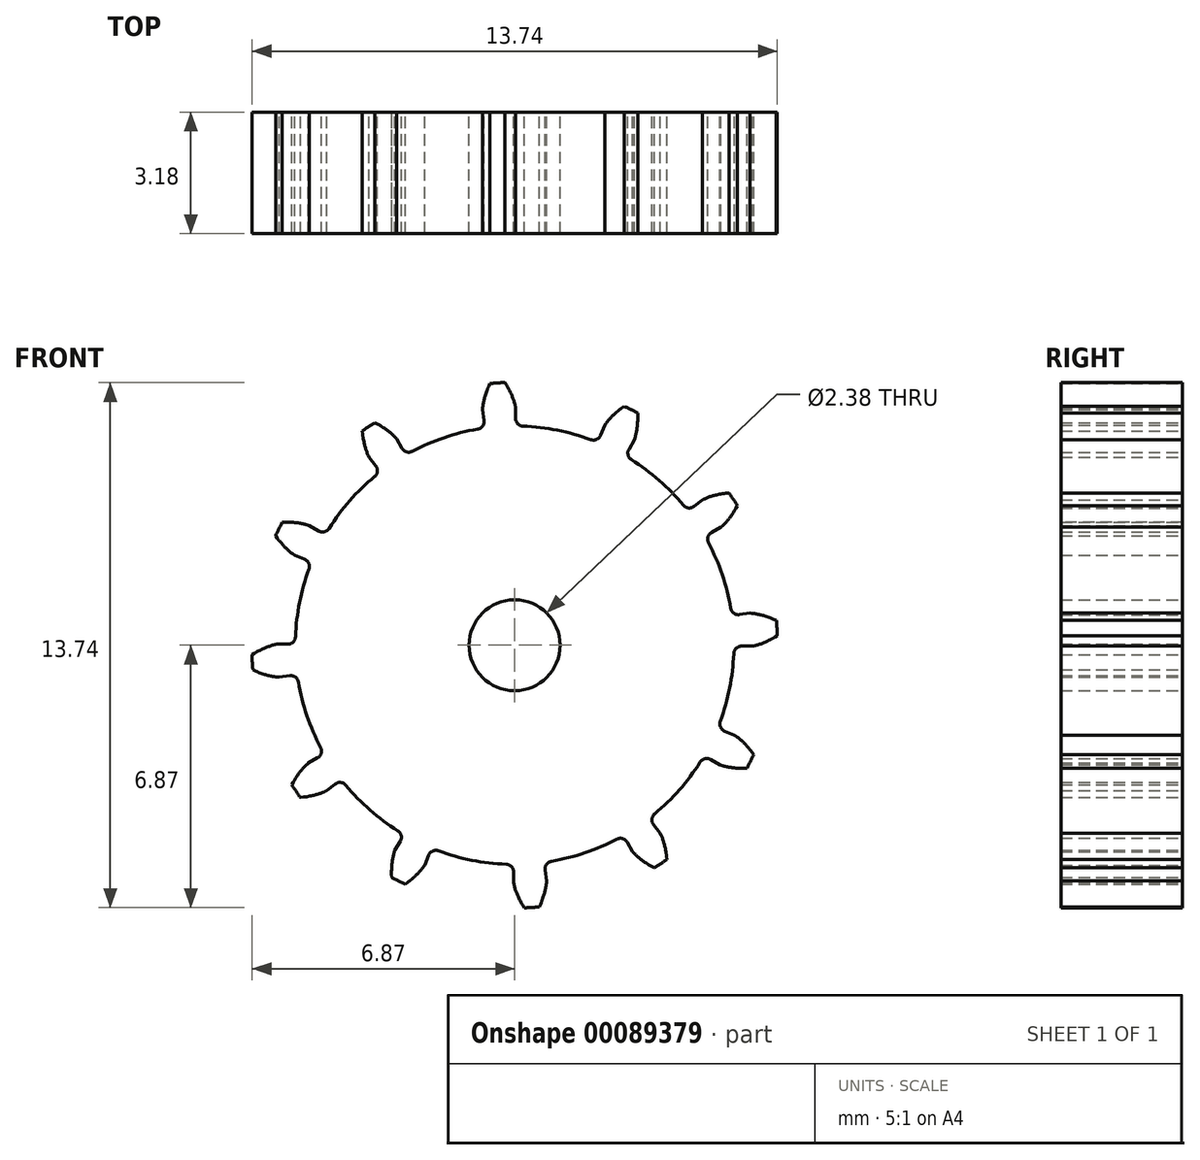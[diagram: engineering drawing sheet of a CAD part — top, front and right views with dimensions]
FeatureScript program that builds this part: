
annotation { "Feature Type Name" : "Feature", "Feature Type Description" : "" }
export const myFeature = defineFeature(function(context is Context, id is Id, definition is map)
    precondition{}
    {
        {
            assignVariable(context, id + "F0", {"name" : "Teeth", "anyValue" : 12});
        }
        {
            var Q0;
            Q0=qCreatedBy(makeId("Front.planeOp"),FACE);
            var sketch = newSketch(context, id + "F1", { "sketchPlane" : qUnion([Q0])});
            skCircle(sketch, "E0", {"center": v(0, 0) * mm, "radius": 6.15 * mm, "construction": true});
            skLineSegment(sketch, "E1", {"start": v(0, 0) * mm, "end": v(-0.28, 6.14) * mm, "construction": true});
            skLineSegment(sketch, "E2", {"start": v(0, 0) * mm, "end": v(-0.59, 6.12) * mm, "construction": true});
            skLineSegment(sketch, "E3", {"start": v(0, 0) * mm, "end": v(-0.9, 6.08) * mm, "construction": true});
            skLineSegment(sketch, "E4", {"start": v(-0.9, 6.08) * mm, "end": v(0.03, 6.22) * mm, "construction": true});
            skLineSegment(sketch, "E5", {"start": v(0, 0) * mm, "end": v(-1.2, 6.03) * mm, "construction": true});
            skLineSegment(sketch, "E6", {"start": v(-1.2, 6.03) * mm, "end": v(0.02, 6.27) * mm, "construction": true});
            skLineSegment(sketch, "E7", {"start": v(-0.9, 6.08) * mm, "end": v(-0.59, 6.12) * mm, "construction": true});
            skLineSegment(sketch, "E8", {"start": v(-1.2, 6.03) * mm, "end": v(-0.9, 6.08) * mm, "construction": true});
            skLineSegment(sketch, "E9", {"start": v(-0.9, 6.08) * mm, "end": v(-0.28, 6.14) * mm, "construction": true});
            skLineSegment(sketch, "E10", {"start": v(-1.2, 6.03) * mm, "end": v(-0.28, 6.14) * mm, "construction": true});
            skLineSegment(sketch, "E11", {"start": v(0, 0) * mm, "end": v(-2.1, 5.78) * mm, "construction": true});
            skLineSegment(sketch, "E12", {"start": v(-2.1, 5.78) * mm, "end": v(-0.07, 6.52) * mm, "construction": true});
            skLineSegment(sketch, "E13", {"start": v(0, 0) * mm, "end": v(-1.81, 5.87) * mm, "construction": true});
            skLineSegment(sketch, "E14", {"start": v(-1.81, 5.87) * mm, "end": v(-0.03, 6.42) * mm, "construction": true});
            skLineSegment(sketch, "E15", {"start": v(0, 0) * mm, "end": v(-1.51, 5.96) * mm, "construction": true});
            skLineSegment(sketch, "E16", {"start": v(-1.51, 5.96) * mm, "end": v(0, 6.34) * mm, "construction": true});
            skLineSegment(sketch, "E17", {"start": v(-1.51, 5.96) * mm, "end": v(-1.2, 6.03) * mm, "construction": true});
            skLineSegment(sketch, "E18", {"start": v(-1.51, 5.96) * mm, "end": v(-1.81, 5.87) * mm, "construction": true});
            skLineSegment(sketch, "E19", {"start": v(-1.81, 5.87) * mm, "end": v(-2.1, 5.78) * mm, "construction": true});
            skLineSegment(sketch, "E20", {"start": v(-1.51, 5.96) * mm, "end": v(-0.28, 6.14) * mm, "construction": true});
            skLineSegment(sketch, "E21", {"start": v(-1.81, 5.87) * mm, "end": v(-0.28, 6.14) * mm, "construction": true});
            skLineSegment(sketch, "E22", {"start": v(-2.1, 5.78) * mm, "end": v(-0.28, 6.14) * mm, "construction": true});
            skLineSegment(sketch, "E23", {"start": v(0, 0) * mm, "end": v(-2.68, 5.53) * mm, "construction": true});
            skLineSegment(sketch, "E24", {"start": v(-2.68, 5.53) * mm, "end": v(-0.18, 6.75) * mm, "construction": true});
            skLineSegment(sketch, "E25", {"start": v(0, 0) * mm, "end": v(-2.96, 5.39) * mm, "construction": true});
            skLineSegment(sketch, "E26", {"start": v(-2.96, 5.39) * mm, "end": v(-0.25, 6.87) * mm, "construction": true});
            skLineSegment(sketch, "E27", {"start": v(0, 0) * mm, "end": v(-3.23, 5.23) * mm, "construction": true});
            skLineSegment(sketch, "E28", {"start": v(0, 0) * mm, "end": v(-2.4, 5.66) * mm, "construction": true});
            skLineSegment(sketch, "E29", {"start": v(-2.4, 5.66) * mm, "end": v(-0.11, 6.63) * mm, "construction": true});
            skLineSegment(sketch, "E30", {"start": v(-2.1, 5.78) * mm, "end": v(-2.4, 5.66) * mm, "construction": true});
            skLineSegment(sketch, "E31", {"start": v(-2.4, 5.66) * mm, "end": v(-2.68, 5.53) * mm, "construction": true});
            skLineSegment(sketch, "E32", {"start": v(-2.68, 5.53) * mm, "end": v(-2.96, 5.39) * mm, "construction": true});
            skLineSegment(sketch, "E33", {"start": v(-2.96, 5.39) * mm, "end": v(-3.23, 5.23) * mm, "construction": true});
            skLineSegment(sketch, "E34", {"start": v(-0.28, 6.14) * mm, "end": v(-2.4, 5.66) * mm, "construction": true});
            skLineSegment(sketch, "E35", {"start": v(-0.28, 6.14) * mm, "end": v(-2.68, 5.53) * mm, "construction": true});
            skLineSegment(sketch, "E36", {"start": v(-0.28, 6.14) * mm, "end": v(-2.96, 5.39) * mm, "construction": true});
            skLineSegment(sketch, "E37", {"start": v(-0.28, 6.14) * mm, "end": v(-3.23, 5.23) * mm, "construction": true});
            skCircle(sketch, "E38", {"center": v(0, 0) * mm, "radius": 6.35 * mm, "construction": true});
            skCircle(sketch, "E39", {"center": v(0, 0) * mm, "radius": 6.88 * mm});
            skPoint(sketch, "E40", {"position": v(0, 6.35) * mm});
            skLineSegment(sketch, "E41", {"start": v(0, 0) * mm, "end": v(-0.56, 8.58) * mm, "construction": true});
            skPoint(sketch, "E42.MirrorP", {"position": v(-0.83, 6.3) * mm});
            skLineSegment(sketch, "E43", {"start": v(-0.83, 6.3) * mm, "end": v(0, 0) * mm, "construction": true});
            skLineSegment(sketch, "E44", {"start": v(0, 0) * mm, "end": v(0, 6.35) * mm, "construction": true});
            skLineSegment(sketch, "E45", {"start": v(-0.59, 6.12) * mm, "end": v(-0.28, 6.14) * mm, "construction": true});
            skLineSegment(sketch, "E46", {"start": v(0.03, 6.22) * mm, "end": v(0.02, 6.27) * mm, "construction": true});
            skLineSegment(sketch, "E47", {"start": v(0, 0) * mm, "end": v(0, 10.19) * mm, "construction": true});
            skCircle(sketch, "E48", {"center": v(0, 0) * mm, "radius": 5.74 * mm});
            skSolve(sketch);
        }
        {
            var Q0;
            Q0=qCreatedBy(makeId("Front.planeOp"),FACE);
            var sketch = newSketch(context, id + "F2", { "sketchPlane" : qUnion([Q0])});
            skCircle(sketch, "E49.0", {"center": v(0, 0) * mm, "radius": 6.35 * mm, "construction": true});
            skPoint(sketch, "E50.0", {"position": v(-0.25, 6.87) * mm});
            skPoint(sketch, "E50.1", {"position": v(-0.18, 6.75) * mm});
            skPoint(sketch, "E50.2", {"position": v(-0.11, 6.63) * mm});
            skPoint(sketch, "E50.3", {"position": v(-0.07, 6.52) * mm});
            skPoint(sketch, "E50.4", {"position": v(-0.03, 6.42) * mm});
            skPoint(sketch, "E50.6", {"position": v(0.02, 6.27) * mm});
            skPoint(sketch, "E50.7", {"position": v(0.03, 6.22) * mm});
            skPoint(sketch, "E50.8", {"position": v(0, 6.34) * mm});
            skLineSegment(sketch, "E51.0", {"start": v(0, 0) * mm, "end": v(-0.56, 8.58) * mm, "construction": true});
            skFitSpline(sketch, "E52", {"points": [v(-0.25, 6.87) * mm, v(-0.18, 6.75) * mm, v(-0.11, 6.63) * mm, v(-0.07, 6.52) * mm, v(-0.03, 6.42) * mm, v(0, 6.34) * mm, v(0.02, 6.27) * mm, v(0.03, 6.22) * mm], "startDerivative": vector(1.31, -2.2) * mm, "endDerivative": vector(0.3, -1.53) * mm});
            skFitSpline(sketch, "E53.MirrorCS", {"points": [v(-0.65, 6.85) * mm, v(-0.7, 6.71) * mm, v(-0.75, 6.59) * mm, v(-0.79, 6.47) * mm, v(-0.8, 6.37) * mm, v(-0.83, 6.29) * mm, v(-0.83, 6.22) * mm, v(-0.84, 6.16) * mm], "startDerivative": vector(-1.01, -2.36) * mm, "endDerivative": vector(-0.1, -1.56) * mm});
            skCircle(sketch, "E54", {"center": v(0, 0) * mm, "radius": 1.2 * mm});
            skCircle(sketch, "E55.0", {"center": v(0, 0) * mm, "radius": 5.74 * mm});
            skArc(sketch, "E56", {"start": v(-0.25, 6.87) * mm, "mid": v(-0.45, 6.86) * mm, "end": v(-0.65, 6.85) * mm});
            skLineSegment(sketch, "E57", {"start": v(-0.84, 6.16) * mm, "end": v(0, 0) * mm});
            skLineSegment(sketch, "E58", {"start": v(0, 0) * mm, "end": v(0.03, 6.22) * mm});
            skSolve(sketch);
        }
        {
            var Q0;
            {var subQ1=sQuery(id+"F2.wireOp",EDGE,"E52");var subQ9=sQuery(id+"F2.wireOp",EDGE,"rA0usyOi-Jm6w-jZNR-JSDv-ujEcH4bsm2Ol");var subQ11=makeQuery(id+"F2.imprint","INTERSECT",VERTEX,{"derivedFrom":[subQ1,subQ9]});Q0=makeQuery(id+"F2.imprint","IMPRINT",FACE,{"disambiguationData":[TD([[makeQuery(id+"F2.imprint","IMPRINT",EDGE,{"disambiguationData":[TD([[subQ11,1.0]])],"derivedFrom":subQ1}),-1.0]])]});}
            var Q1;
            {var subQ0=sQuery(id+"F2.wireOp",EDGE,"QqPcIgQ4-TZE6-73E5-WQaq-ugCT5JtziKyn");var subQ1=sQuery(id+"F2.wireOp",EDGE,"90be38e0-c88f-493d-85a8-1201295b9109.0");var subQ2=makeQuery(id+"F2.imprint","INTERSECT",VERTEX,{"derivedFrom":[subQ1,subQ0]});Q1=makeQuery(id+"F2.imprint","IMPRINT",FACE,{"disambiguationData":[TD([[makeQuery(id+"F2.imprint","IMPRINT",EDGE,{"disambiguationData":[TD([[subQ2,1.0]])],"derivedFrom":subQ1}),1.0]])]});}
            var Q2;
            {var subQ0=sQuery(id+"F2.wireOp",EDGE,"QqPcIgQ4-TZE6-73E5-WQaq-ugCT5JtziKyn");var subQ1=sQuery(id+"F2.wireOp",EDGE,"90be38e0-c88f-493d-85a8-1201295b9109.0");var subQ2=makeQuery(id+"F2.imprint","INTERSECT",VERTEX,{"derivedFrom":[subQ1,subQ0]});Q2=makeQuery(id+"F2.imprint","IMPRINT",FACE,{"disambiguationData":[TD([[makeQuery(id+"F2.imprint","IMPRINT",EDGE,{"disambiguationData":[TD([[subQ2,-1.0]])],"derivedFrom":subQ1}),1.0]])]});}
            var Q3;
            {var subQ1=sQuery(id+"F2.wireOp",EDGE,"E52");var subQ8=sQuery(id+"F2.wireOp",EDGE,"b861a5ab-cd51-40f1-92ab-cea0f5fe0d4d.1");var subQ11=makeQuery(id+"F2.imprint","INTERSECT",VERTEX,{"derivedFrom":[subQ1,subQ8]});Q3=makeQuery(id+"F2.imprint","IMPRINT",FACE,{"disambiguationData":[TD([[makeQuery(id+"F2.imprint","IMPRINT",EDGE,{"disambiguationData":[TD([[subQ11,1.0]])],"derivedFrom":subQ1}),-1.0]])]});}
            var Q4;
            {var subQ0=sQuery(id+"F2.wireOp",EDGE,"b861a5ab-cd51-40f1-92ab-cea0f5fe0d4d.0");var subQ1=sQuery(id+"F2.wireOp",EDGE,"E54");var subQ2=makeQuery(id+"F2.imprint","INTERSECT",VERTEX,{"derivedFrom":[subQ1,subQ0]});Q4=makeQuery(id+"F2.imprint","IMPRINT",FACE,{"disambiguationData":[TD([[makeQuery(id+"F2.imprint","IMPRINT",EDGE,{"disambiguationData":[TD([[subQ2,-1.0]])],"derivedFrom":subQ1}),-1.0]])]});}
            var Q5;
            {var subQ0=sQuery(id+"F2.wireOp",EDGE,"b861a5ab-cd51-40f1-92ab-cea0f5fe0d4d.0");var subQ1=sQuery(id+"F2.wireOp",EDGE,"E54");var subQ2=makeQuery(id+"F2.imprint","INTERSECT",VERTEX,{"derivedFrom":[subQ1,subQ0]});Q5=makeQuery(id+"F2.imprint","IMPRINT",FACE,{"disambiguationData":[TD([[makeQuery(id+"F2.imprint","IMPRINT",EDGE,{"disambiguationData":[TD([[subQ2,1.0]])],"derivedFrom":subQ1}),-1.0]])]});}
            extrude(context, id + "F3", {"entities" : qUnion([Q0, Q1, Q2, Q3, Q4, Q5]), "depth" : 3.17 * mm});
        }
        {
            var Q0;
            Q0=makeQuery(id+"F3.opExtrude","SWEPT_EDGE",EDGE,{"disambiguationData":[OSD([sQuery(id+"F2.wireOp",EDGE,"b861a5ab-cd51-40f1-92ab-cea0f5fe0d4d.1"),sQuery(id+"F2.wireOp",EDGE,"E55.0")])]});
            var Q1;
            Q1=makeQuery(id+"F3.opExtrude","SWEPT_EDGE",EDGE,{"disambiguationData":[OSD([sQuery(id+"F2.wireOp",EDGE,"b861a5ab-cd51-40f1-92ab-cea0f5fe0d4d.0"),sQuery(id+"F2.wireOp",EDGE,"E55.0")])]});
            fillet(context, id + "F4", {"entities" : qUnion([Q0, Q1]), "radius" : 0.2 * mm, "tangentPropagation" : true, "allowEdgeOverflow" : false});
        }
        {
            var Q0;
            Q0=makeQuery(id+"F4.opFillet","BLEND_FACE",FACE,{"disambiguationData":[OSD([sQuery(id+"F2.wireOp",EDGE,"E55.0"),sQuery(id+"F2.wireOp",EDGE,"E57")])]});
            var Q1;
            Q1=makeQuery(id+"F3.opExtrude","SWEPT_FACE",FACE,{"disambiguationData":[OSD([sQuery(id+"F2.wireOp",EDGE,"E57")])]});
            var Q2;
            Q2=makeQuery(id+"F3.opExtrude","SWEPT_FACE",FACE,{"disambiguationData":[OSD([sQuery(id+"F2.wireOp",EDGE,"E53.MirrorCS")])]});
            var Q3;
            Q3=makeQuery(id+"F3.opExtrude","SWEPT_FACE",FACE,{"disambiguationData":[OSD([sQuery(id+"F2.wireOp",EDGE,"E56")])]});
            var Q4;
            Q4=makeQuery(id+"F3.opExtrude","SWEPT_FACE",FACE,{"disambiguationData":[OSD([sQuery(id+"F2.wireOp",EDGE,"E52")])]});
            var Q5;
            Q5=makeQuery(id+"F3.opExtrude","SWEPT_FACE",FACE,{"disambiguationData":[OSD([sQuery(id+"F2.wireOp",EDGE,"E58")])]});
            var Q6;
            Q6=makeQuery(id+"F4.opFillet","BLEND_FACE",FACE,{"disambiguationData":[OSD([sQuery(id+"F2.wireOp",EDGE,"E55.0"),sQuery(id+"F2.wireOp",EDGE,"E58")])]});
            var Q7;
            Q7=makeQuery(id+"F3.opExtrude","SWEPT_FACE",FACE,{"disambiguationData":[OSD([sQuery(id+"F2.wireOp",EDGE,"E55.0")])]});
            circularPattern(context, id + "F5", {"faces" : qUnion([Q0, Q1, Q2, Q3, Q4, Q5, Q6]), "axis" : qUnion([Q7]), "angle" : 360 * degree, "instanceCount" : round(getVariable(context, 'Teeth')), "equalSpace" : true, "patternType" : PatternType.FACE});
        }
    });
